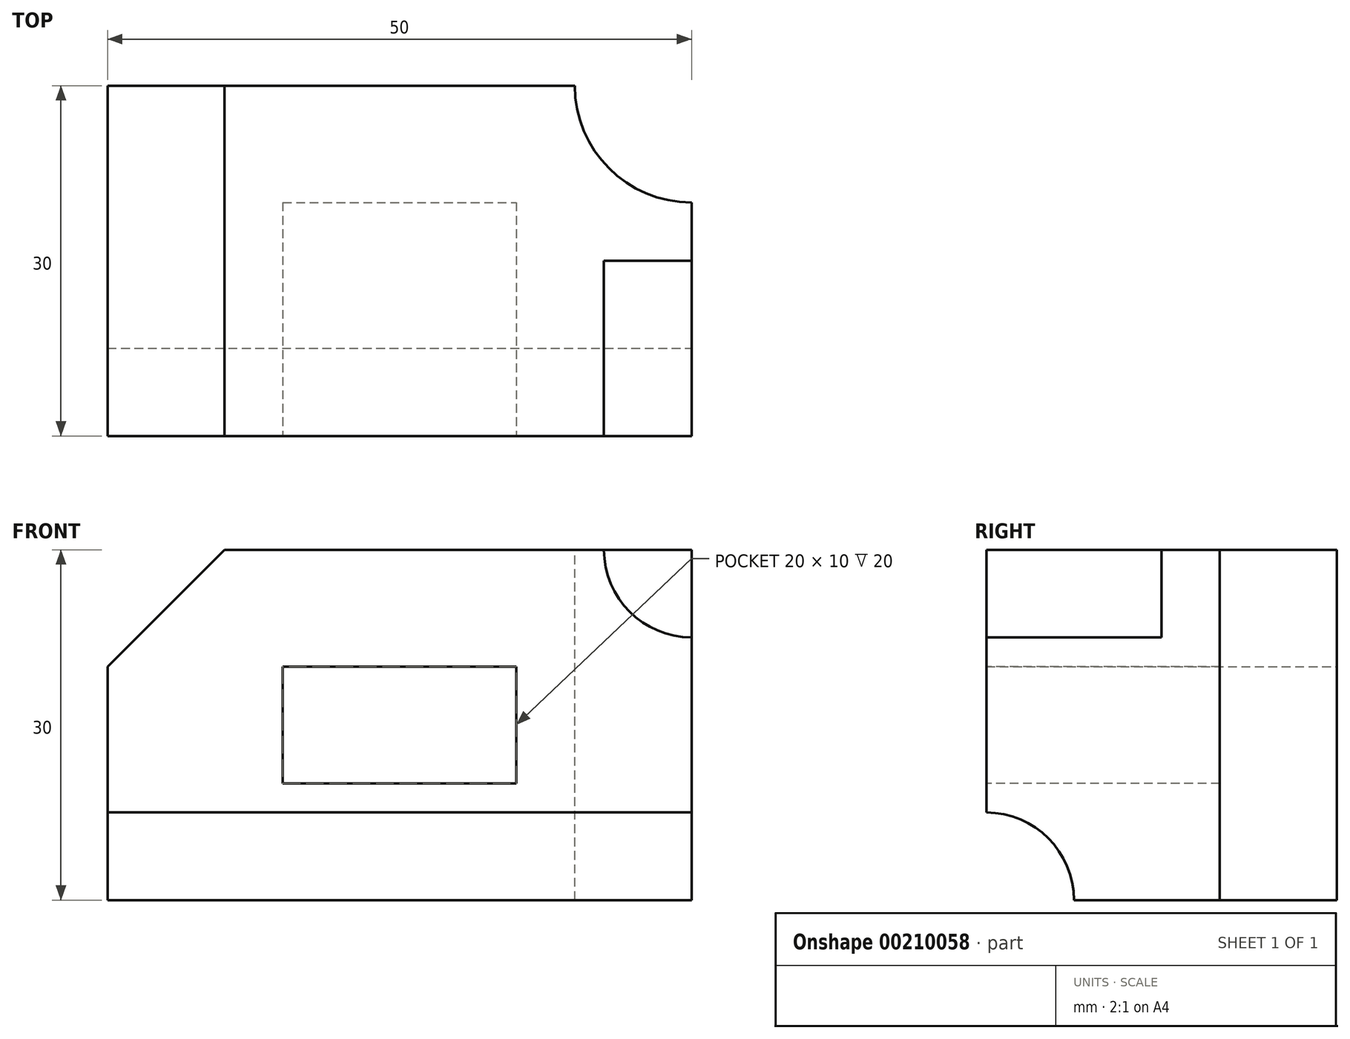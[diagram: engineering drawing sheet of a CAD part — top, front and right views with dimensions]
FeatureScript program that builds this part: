
annotation { "Feature Type Name" : "Feature", "Feature Type Description" : "" }
export const myFeature = defineFeature(function(context is Context, id is Id, definition is map)
    precondition{}
    {
        {
            var Q0;
            Q0=qCreatedBy(makeId("Front.planeOp"),FACE);
            var sketch = newSketch(context, id + "F0", { "sketchPlane" : qUnion([Q0])});
            skLineSegment(sketch, "E0.bottom", {"start": v(0, 0) * mm, "end": v(50, 0) * mm});
            skLineSegment(sketch, "E0.top", {"start": v(0, 30) * mm, "end": v(50, 30) * mm});
            skLineSegment(sketch, "E0.left", {"start": v(0, 0) * mm, "end": v(0, 30) * mm});
            skLineSegment(sketch, "E0.right", {"start": v(50, 0) * mm, "end": v(50, 30) * mm});
            skSolve(sketch);
        }
        {
            var Q0;
            Q0 = qSketchRegion(id + "F0", true);
            extrude(context, id + "F1", {"entities" : qUnion([Q0]), "oppositeDirection" : true, "depth" : 30 * mm});
        }
        {
            var Q0;
            Q0=makeQuery(id+"F1.opExtrude","SWEPT_EDGE",EDGE,{"disambiguationData":[OSD([sQuery(id+"F0.wireOp",EDGE,"E0.top"),sQuery(id+"F0.wireOp",EDGE,"E0.left")])]});
            chamfer(context, id + "F2", {"entities" : qUnion([Q0]), "width" : 10 * mm, "tangentPropagation" : true});
        }
        {
            var Q0;
            Q0=makeQuery(id+"F1.opExtrude","CAP_FACE",FACE,{"disambiguationData":[OSD([sQuery(id+"F0.wireOp",EDGE,"E0.bottom"),sQuery(id+"F0.wireOp",EDGE,"E0.top"),sQuery(id+"F0.wireOp",EDGE,"E0.left"),sQuery(id+"F0.wireOp",EDGE,"E0.right")])],"isStart":true});
            var sketch = newSketch(context, id + "F3", { "sketchPlane" : qUnion([Q0])});
            skLineSegment(sketch, "E1.bottom", {"start": v(15, 20) * mm, "end": v(35, 20) * mm});
            skLineSegment(sketch, "E1.top", {"start": v(15, 10) * mm, "end": v(35, 10) * mm});
            skLineSegment(sketch, "E1.left", {"start": v(15, 20) * mm, "end": v(15, 10) * mm});
            skLineSegment(sketch, "E1.right", {"start": v(35, 20) * mm, "end": v(35, 10) * mm});
            skSolve(sketch);
        }
        {
            var Q0;
            Q0 = qSketchRegion(id + "F3", true);
            extrude(context, id + "F4", {"entities" : qUnion([Q0]), "operationType" : NewBodyOperationType.REMOVE, "oppositeDirection" : true, "depth" : 20 * mm});
        }
        {
            var Q0;
            Q0=makeQuery(id+"F1.opExtrude","CAP_FACE",FACE,{"disambiguationData":[OSD([sQuery(id+"F0.wireOp",EDGE,"E0.bottom"),sQuery(id+"F0.wireOp",EDGE,"E0.top"),sQuery(id+"F0.wireOp",EDGE,"E0.left"),sQuery(id+"F0.wireOp",EDGE,"E0.right")])],"isStart":true});
            var sketch = newSketch(context, id + "F5", { "sketchPlane" : qUnion([Q0])});
            skCircle(sketch, "E2", {"center": v(50, 30) * mm, "radius": 7.5 * mm});
            skSolve(sketch);
        }
        {
            var Q0;
            Q0 = qSketchRegion(id + "F5", true);
            extrude(context, id + "F6", {"entities" : qUnion([Q0]), "operationType" : NewBodyOperationType.REMOVE, "oppositeDirection" : true, "depth" : 15 * mm});
        }
        {
            var Q0;
            Q0=makeQuery(id+"F1.opExtrude","SWEPT_FACE",FACE,{"disambiguationData":[OSD([sQuery(id+"F0.wireOp",EDGE,"E0.top")])]});
            var sketch = newSketch(context, id + "F7", { "sketchPlane" : qUnion([Q0])});
            skCircle(sketch, "E3", {"center": v(50, 30) * mm, "radius": 10 * mm});
            skSolve(sketch);
        }
        {
            var Q0;
            Q0 = qSketchRegion(id + "F7", true);
            extrude(context, id + "F8", {"entities" : qUnion([Q0]), "operationType" : NewBodyOperationType.REMOVE, "endBound" : BoundingType.THROUGH_ALL, "oppositeDirection" : true, "depth" : 25 * mm});
        }
        {
            var Q0;
            Q0=makeQuery(id+"F1.opExtrude","SWEPT_FACE",FACE,{"disambiguationData":[OSD([sQuery(id+"F0.wireOp",EDGE,"E0.right")])]});
            var sketch = newSketch(context, id + "F9", { "sketchPlane" : qUnion([Q0])});
            skCircle(sketch, "E4", {"center": v(0, 0) * mm, "radius": 7.5 * mm});
            skSolve(sketch);
        }
        {
            var Q0;
            Q0 = qSketchRegion(id + "F9", true);
            extrude(context, id + "F10", {"entities" : qUnion([Q0]), "operationType" : NewBodyOperationType.REMOVE, "endBound" : BoundingType.THROUGH_ALL, "oppositeDirection" : true, "depth" : 25 * mm});
        }
    });
